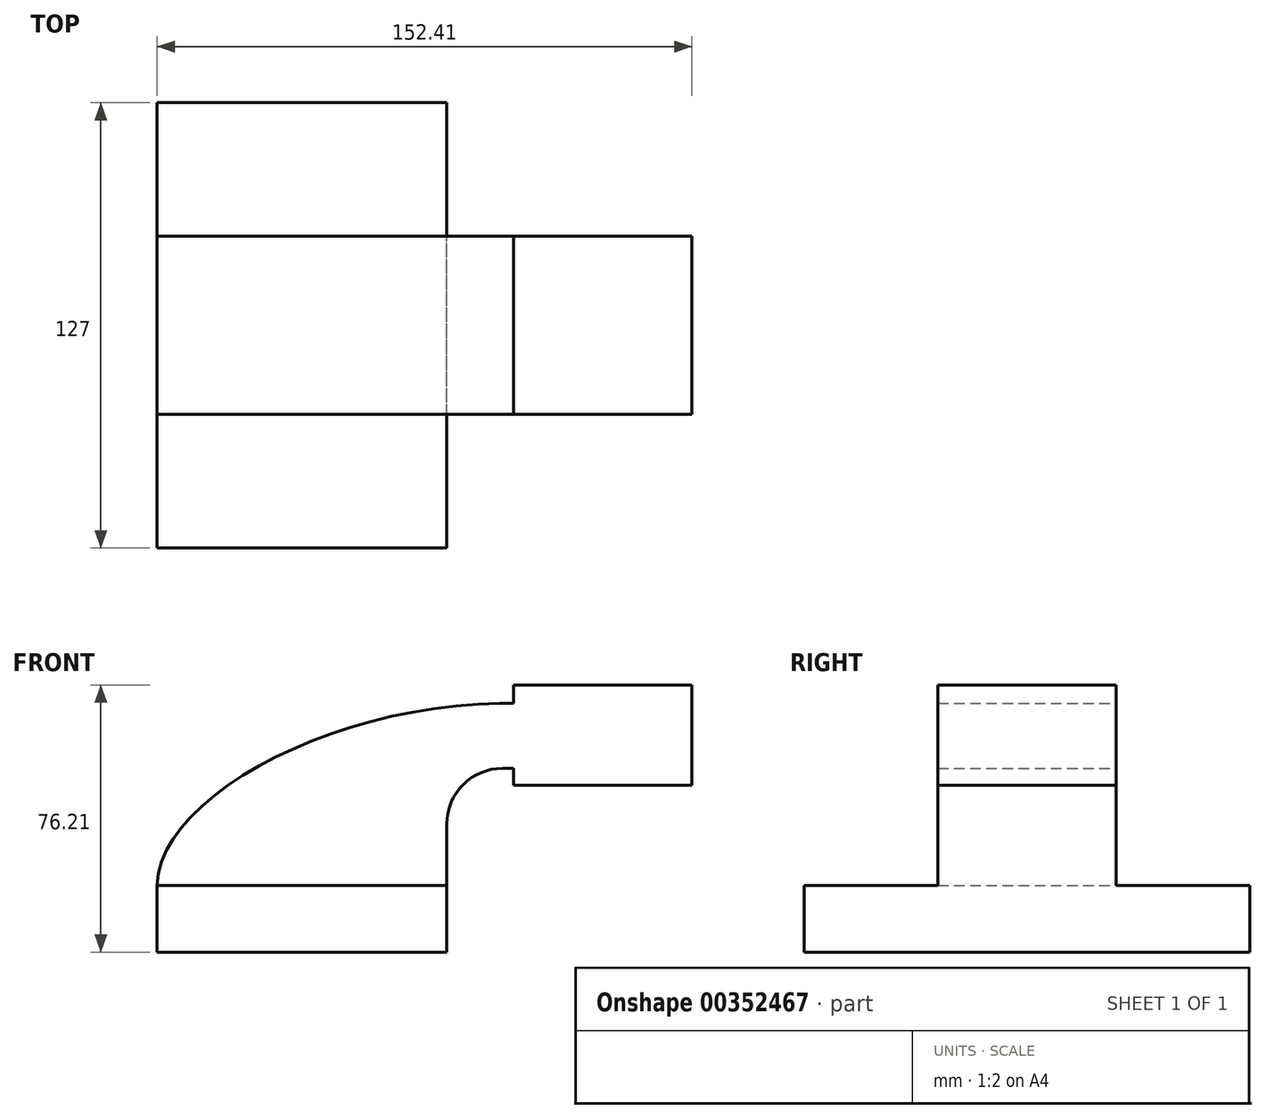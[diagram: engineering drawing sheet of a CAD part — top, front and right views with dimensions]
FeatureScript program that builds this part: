
annotation { "Feature Type Name" : "Feature", "Feature Type Description" : "" }
export const myFeature = defineFeature(function(context is Context, id is Id, definition is map)
    precondition{}
    {
        {
            var Q0;
            Q0=qCreatedBy(makeId("Front.planeOp"),FACE);
            var sketch = newSketch(context, id + "F0", { "sketchPlane" : qUnion([Q0])});
            skLineSegment(sketch, "E0.bottom", {"start": v(-41.28, -9.53) * mm, "end": v(41.28, -9.53) * mm});
            skLineSegment(sketch, "E0.top", {"start": v(-41.28, 9.53) * mm, "end": v(41.28, 9.53) * mm});
            skLineSegment(sketch, "E0.left", {"start": v(-41.28, -9.53) * mm, "end": v(-41.28, 9.53) * mm});
            skLineSegment(sketch, "E0.right", {"start": v(41.28, -9.53) * mm, "end": v(41.28, 9.53) * mm});
            skPoint(sketch, "E0.middle", {"position": v(0, 0) * mm});
            skLineSegment(sketch, "E1.bottom", {"start": v(111.12, 38.1) * mm, "end": v(60.32, 38.1) * mm});
            skLineSegment(sketch, "E1.top", {"start": v(111.12, 66.68) * mm, "end": v(60.32, 66.68) * mm});
            skLineSegment(sketch, "E1.left", {"start": v(111.12, 38.1) * mm, "end": v(111.12, 66.67) * mm});
            skLineSegment(sketch, "E1.right", {"start": v(60.32, 38.1) * mm, "end": v(60.32, 66.67) * mm});
            skPoint(sketch, "E1.middle", {"position": v(85.72, 52.39) * mm});
            skLineSegment(sketch, "E2", {"start": v(41.28, 9.52) * mm, "end": v(41.28, 27) * mm});
            skArc(sketch, "E3", {"start": v(41.27, 27) * mm, "mid": v(45.92, 38.23) * mm, "end": v(57.15, 42.88) * mm});
            skLineSegment(sketch, "E4", {"start": v(57.15, 42.88) * mm, "end": v(85.72, 42.88) * mm});
            skLineSegment(sketch, "E5.0", {"start": v(57.15, 61.42) * mm, "end": v(85.72, 61.42) * mm});
            skArc(sketch, "E5.1", {"start": v(22.73, 27) * mm, "mid": v(32.81, 51.34) * mm, "end": v(57.15, 61.42) * mm});
            skLineSegment(sketch, "E5.2", {"start": v(22.73, 9.52) * mm, "end": v(22.73, 27) * mm});
            skLineSegment(sketch, "E6", {"start": v(85.72, 38.1) * mm, "end": v(85.72, 66.68) * mm});
            skFitSpline(sketch, "E7", {"points": [v(-41.28, 9.53) * mm, v(57.15, 61.42) * mm], "startDerivative": vector(2.62, 76.76) * mm, "endDerivative": vector(144.15, 1.2) * mm});
            skSolve(sketch);
        }
        {
            var Q0;
            Q0=makeQuery(id+"F0.imprint","IMPRINT",FACE,{"disambiguationData":[TD([[makeQuery(id+"F0.imprint","IMPRINT",EDGE,{"derivedFrom":sQuery(id+"F0.wireOp",EDGE,"E0.bottom")}),1.0]])]});
            extrude(context, id + "F1", {"entities" : qUnion([Q0]), "endBound" : BoundingType.SYMMETRIC, "depth" : 127 * mm});
        }
        {
            var Q0;
            {var subQ1=sQuery(id+"F0.wireOp",EDGE,"E2");Q0=makeQuery(id+"F0.imprint","IMPRINT",FACE,{"disambiguationData":[TD([[makeQuery(id+"F0.imprint","IMPRINT",EDGE,{"derivedFrom":subQ1}),1.0]])]});}
            extrude(context, id + "F2", {"entities" : qUnion([Q0]), "operationType" : NewBodyOperationType.ADD, "endBound" : BoundingType.SYMMETRIC, "depth" : 50.8 * mm});
        }
        {
            var Q0;
            Q0 = qSketchRegion(id + "F0", true);
            extrude(context, id + "F3", {"entities" : qUnion([Q0]), "operationType" : NewBodyOperationType.ADD, "endBound" : BoundingType.SYMMETRIC, "depth" : 50.8 * mm});
        }
    });
